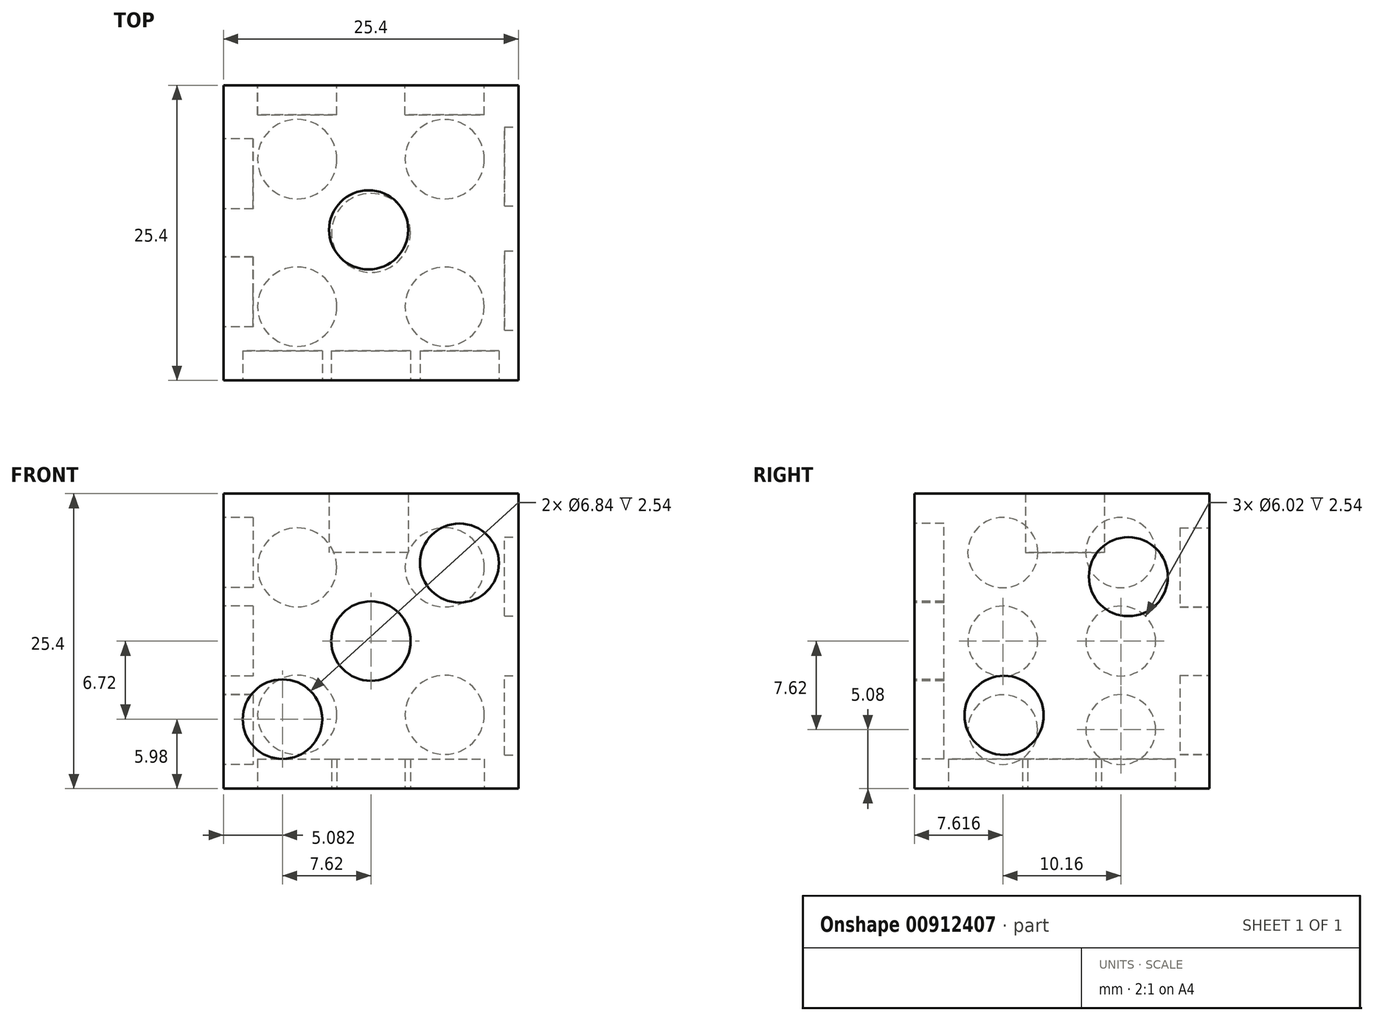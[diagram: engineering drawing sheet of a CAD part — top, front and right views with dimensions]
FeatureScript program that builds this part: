
annotation { "Feature Type Name" : "Feature", "Feature Type Description" : "" }
export const myFeature = defineFeature(function(context is Context, id is Id, definition is map)
    precondition{}
    {
        {
            var Q0;
            Q0=qCreatedBy(makeId("Top.planeOp"),FACE);
            var sketch = newSketch(context, id + "F0", { "sketchPlane" : qUnion([Q0])});
            skLineSegment(sketch, "E0.bottom", {"start": v(-22.93, 8.38) * mm, "end": v(-5.15, 8.38) * mm});
            skLineSegment(sketch, "E0.top", {"start": v(-22.93, -17.02) * mm, "end": v(-5.15, -17.02) * mm});
            skLineSegment(sketch, "E0.left", {"start": v(-26.74, 4.57) * mm, "end": v(-26.74, -13.21) * mm});
            skLineSegment(sketch, "E0.right", {"start": v(-1.34, 4.57) * mm, "end": v(-1.34, -13.21) * mm});
            skLineSegment(sketch, "E1.bottom", {"start": v(-15, 3.03) * mm, "end": v(-14.46, 3.03) * mm});
            skCircle(sketch, "E2", {"center": v(-14.24, -4.06) * mm, "radius": 3.4 * mm});
            skPoint(sketch, "E3.visualSharp", {"position": v(-26.74, 8.38) * mm});
            skPoint(sketch, "E4.visualSharp", {"position": v(-26.74, -17.02) * mm});
            skPoint(sketch, "E5.visualSharp", {"position": v(-1.34, -17.02) * mm});
            skPoint(sketch, "E6.visualSharp", {"position": v(-1.34, 8.38) * mm});
            skLineSegment(sketch, "E7", {"start": v(-26.74, -13.21) * mm, "end": v(-26.74, -17.02) * mm});
            skLineSegment(sketch, "E8", {"start": v(-26.74, -17.02) * mm, "end": v(-22.93, -17.02) * mm});
            skLineSegment(sketch, "E9", {"start": v(-1.34, -17.02) * mm, "end": v(-1.34, -13.21) * mm});
            skLineSegment(sketch, "E10", {"start": v(-5.15, -17.02) * mm, "end": v(-1.34, -17.02) * mm});
            skLineSegment(sketch, "E11", {"start": v(-1.34, 4.57) * mm, "end": v(-1.34, 8.38) * mm});
            skLineSegment(sketch, "E12", {"start": v(-4.55, 8.33) * mm, "end": v(-5.15, 8.38) * mm});
            skLineSegment(sketch, "E13", {"start": v(-1.34, 8.38) * mm, "end": v(-5.15, 8.38) * mm});
            skLineSegment(sketch, "E14", {"start": v(-22.93, 8.38) * mm, "end": v(-26.74, 8.38) * mm});
            skLineSegment(sketch, "E15", {"start": v(-26.74, 4.57) * mm, "end": v(-26.74, 8.38) * mm});
            skSolve(sketch);
        }
        {
            var Q0;
            Q0=qSketchRegion(id+"F0",true);
            extrude(context, id + "F1", {"entities" : qUnion([Q0]), "depth" : 25.4 * mm, "offsetDistance" : 25.4 * mm});
        }
        {
            var Q0;
            Q0=qCreatedBy(makeId("Right.planeOp"),FACE);
            var sketch = newSketch(context, id + "F2", { "sketchPlane" : qUnion([Q0])});
            skCircle(sketch, "E16", {"center": v(-9.3, 6.3) * mm, "radius": 3.4 * mm});
            skCircle(sketch, "E17", {"center": v(1.4, 18.25) * mm, "radius": 3.4 * mm});
            skSolve(sketch);
        }
        {
            var Q0;
            Q0=makeQuery(id+"F0.imprint","IMPRINT",FACE,{"disambiguationData":[TD([[makeQuery(id+"F0.imprint","IMPRINT",EDGE,{"derivedFrom":sQuery(id+"F0.wireOp",EDGE,"E2")}),1.0]])]});
            extrude(context, id + "F3", {"entities" : qUnion([Q0]), "operationType" : NewBodyOperationType.ADD, "depth" : 20.32 * mm, "offsetDistance" : 25.4 * mm});
        }
        {
            var Q0;
            Q0=makeQuery(id+"F1.opExtrude","SWEPT_FACE",FACE,{"disambiguationData":[OSD([sQuery(id+"F0.wireOp",EDGE,"E0.top")])]});
            var sketch = newSketch(context, id + "F4", { "sketchPlane" : qUnion([Q0])});
            skCircle(sketch, "E18", {"center": v(-21.66, 5.98) * mm, "radius": 3.42 * mm});
            skCircle(sketch, "E19", {"center": v(-6.42, 19.42) * mm, "radius": 3.4 * mm});
            skCircle(sketch, "E20", {"center": v(-14.04, 12.7) * mm, "radius": 3.42 * mm});
            skSolve(sketch);
        }
        {
            var Q0;
            Q0=makeQuery(id+"F4.imprint","IMPRINT",FACE,{"disambiguationData":[TD([[makeQuery(id+"F4.imprint","IMPRINT",EDGE,{"derivedFrom":sQuery(id+"F4.wireOp",EDGE,"E18")}),1.0]])]});
            var Q1;
            Q1=makeQuery(id+"F4.imprint","IMPRINT",FACE,{"disambiguationData":[TD([[makeQuery(id+"F4.imprint","IMPRINT",EDGE,{"derivedFrom":sQuery(id+"F4.wireOp",EDGE,"E20")}),1.0]])]});
            var Q2;
            Q2=makeQuery(id+"F4.imprint","IMPRINT",FACE,{"disambiguationData":[TD([[makeQuery(id+"F4.imprint","IMPRINT",EDGE,{"derivedFrom":sQuery(id+"F4.wireOp",EDGE,"E19")}),1.0]])]});
            extrude(context, id + "F5", {"entities" : qUnion([Q0, Q1, Q2]), "operationType" : NewBodyOperationType.REMOVE, "oppositeDirection" : true, "depth" : 2.54 * mm, "offsetDistance" : 25.4 * mm});
        }
        {
            var Q0;
            Q0=makeQuery(id+"F1.opExtrude","SWEPT_FACE",FACE,{"disambiguationData":[OSD([sQuery(id+"F0.wireOp",EDGE,"E0.bottom")])]});
            var sketch = newSketch(context, id + "F6", { "sketchPlane" : qUnion([Q0])});
            skLineSegment(sketch, "E21", {"start": v(14.04, 25.4) * mm, "end": v(14.04, 0) * mm});
            skPoint(sketch, "E22.endSnap0", {"position": v(20.39, 19.05) * mm});
            skPoint(sketch, "E23.endSnap0", {"position": v(7.69, 6.35) * mm});
            skCircle(sketch, "E24", {"center": v(7.69, 6.35) * mm, "radius": 3.4 * mm});
            skCircle(sketch, "E25", {"center": v(20.39, 6.35) * mm, "radius": 3.4 * mm});
            skCircle(sketch, "E26", {"center": v(20.39, 19.05) * mm, "radius": 3.4 * mm});
            skCircle(sketch, "E27", {"center": v(7.69, 19.05) * mm, "radius": 3.4 * mm});
            skSolve(sketch);
        }
        {
            var Q0;
            Q0=makeQuery(id+"F6.imprint","IMPRINT",FACE,{"disambiguationData":[TD([[makeQuery(id+"F6.imprint","IMPRINT",EDGE,{"derivedFrom":sQuery(id+"F6.wireOp",EDGE,"E27")}),1.0]])]});
            var Q1;
            Q1=makeQuery(id+"F6.imprint","IMPRINT",FACE,{"disambiguationData":[TD([[makeQuery(id+"F6.imprint","IMPRINT",EDGE,{"derivedFrom":sQuery(id+"F6.wireOp",EDGE,"E25")}),1.0]])]});
            var Q2;
            Q2=makeQuery(id+"F6.imprint","IMPRINT",FACE,{"disambiguationData":[TD([[makeQuery(id+"F6.imprint","IMPRINT",EDGE,{"derivedFrom":sQuery(id+"F6.wireOp",EDGE,"E26")}),1.0]])]});
            var Q3;
            Q3=makeQuery(id+"F6.imprint","IMPRINT",FACE,{"disambiguationData":[TD([[makeQuery(id+"F6.imprint","IMPRINT",EDGE,{"derivedFrom":sQuery(id+"F6.wireOp",EDGE,"E24")}),1.0]])]});
            extrude(context, id + "F7", {"entities" : qUnion([Q0, Q1, Q2, Q3]), "operationType" : NewBodyOperationType.REMOVE, "oppositeDirection" : true, "depth" : 2.54 * mm, "offsetDistance" : 25.4 * mm});
        }
        {
            var Q0;
            {var subQ0=sQuery(id+"F0.wireOp",EDGE,"E2");Q0=makeQuery(id+"F3.boolean.opBoolean","MERGE",FACE,{"derivedFrom":[makeQuery(id+"F1.opExtrude","CAP_FACE",FACE,{"disambiguationData":[OSD([sQuery(id+"F0.wireOp",EDGE,"E0.bottom"),sQuery(id+"F0.wireOp",EDGE,"E0.top"),sQuery(id+"F0.wireOp",EDGE,"E0.left"),sQuery(id+"F0.wireOp",EDGE,"E0.right"),subQ0])],"isStart":true}),makeQuery(id+"F3.opExtrude","CAP_FACE",FACE,{"disambiguationData":[OSD([subQ0])],"isStart":true})]});}
            var sketch = newSketch(context, id + "F8", { "sketchPlane" : qUnion([Q0])});
            skPoint(sketch, "E28.oppositeSnap0", {"position": v(-26.74, 4.32) * mm});
            skCircle(sketch, "E29", {"center": v(-14.04, 4.32) * mm, "radius": 3.4 * mm});
            skPoint(sketch, "E30.endSnap0", {"position": v(-14.04, -8.38) * mm});
            skCircle(sketch, "E31", {"center": v(-20.39, 10.67) * mm, "radius": 3.42 * mm});
            skCircle(sketch, "E32", {"center": v(-7.69, 10.67) * mm, "radius": 3.4 * mm});
            skCircle(sketch, "E33", {"center": v(-7.69, -2.03) * mm, "radius": 3.42 * mm});
            skCircle(sketch, "E34", {"center": v(-20.39, -2.03) * mm, "radius": 3.42 * mm});
            skLineSegment(sketch, "E35", {"start": v(-14.04, 4.32) * mm, "end": v(-26.74, 4.32) * mm});
            skLineSegment(sketch, "E36", {"start": v(-20.39, 4.32) * mm, "end": v(-20.39, 17.02) * mm});
            skLineSegment(sketch, "E37", {"start": v(-20.39, 4.32) * mm, "end": v(-20.39, -8.38) * mm});
            skLineSegment(sketch, "E38", {"start": v(-14.04, 4.32) * mm, "end": v(-1.34, 4.32) * mm});
            skLineSegment(sketch, "E39", {"start": v(-7.69, 4.32) * mm, "end": v(-7.69, -8.38) * mm});
            skLineSegment(sketch, "E40", {"start": v(-7.69, 4.32) * mm, "end": v(-7.69, 17.02) * mm});
            skSolve(sketch);
        }
        {
            var Q0;
            Q0=qSketchRegion(id+"F8",true);
            extrude(context, id + "F9", {"entities" : qUnion([Q0]), "operationType" : NewBodyOperationType.REMOVE, "oppositeDirection" : true, "depth" : 2.54 * mm, "offsetDistance" : 25.4 * mm});
        }
        {
            var Q0;
            Q0=makeQuery(id+"F1.opExtrude","SWEPT_FACE",FACE,{"disambiguationData":[OSD([sQuery(id+"F0.wireOp",EDGE,"E0.left")])]});
            var sketch = newSketch(context, id + "F10", { "sketchPlane" : qUnion([Q0])});
            skCircle(sketch, "E41", {"center": v(9.4, 20.32) * mm, "radius": 3.02 * mm});
            skCircle(sketch, "E42", {"center": v(-0.76, 5.08) * mm, "radius": 3.01 * mm});
            skCircle(sketch, "E43", {"center": v(-0.76, 12.7) * mm, "radius": 3 * mm});
            skCircle(sketch, "E44", {"center": v(9.4, 12.7) * mm, "radius": 3.01 * mm});
            skCircle(sketch, "E45", {"center": v(-0.76, 20.32) * mm, "radius": 3.02 * mm});
            skCircle(sketch, "E46", {"center": v(9.4, 5.08) * mm, "radius": 3 * mm});
            skSolve(sketch);
        }
        {
            var Q0;
            Q0=makeQuery(id+"F10.imprint","IMPRINT",FACE,{"disambiguationData":[TD([[makeQuery(id+"F10.imprint","IMPRINT",EDGE,{"derivedFrom":sQuery(id+"F10.wireOp",EDGE,"E41")}),1.0]])]});
            var Q1;
            Q1=makeQuery(id+"F10.imprint","IMPRINT",FACE,{"disambiguationData":[TD([[makeQuery(id+"F10.imprint","IMPRINT",EDGE,{"derivedFrom":sQuery(id+"F10.wireOp",EDGE,"E44")}),1.0]])]});
            var Q2;
            Q2=makeQuery(id+"F10.imprint","IMPRINT",FACE,{"disambiguationData":[TD([[makeQuery(id+"F10.imprint","IMPRINT",EDGE,{"derivedFrom":sQuery(id+"F10.wireOp",EDGE,"E43")}),1.0]])]});
            var Q3;
            Q3=makeQuery(id+"F10.imprint","IMPRINT",FACE,{"disambiguationData":[TD([[makeQuery(id+"F10.imprint","IMPRINT",EDGE,{"derivedFrom":sQuery(id+"F10.wireOp",EDGE,"E45")}),1.0]])]});
            var Q4;
            Q4=makeQuery(id+"F10.imprint","IMPRINT",FACE,{"disambiguationData":[TD([[makeQuery(id+"F10.imprint","IMPRINT",EDGE,{"derivedFrom":sQuery(id+"F10.wireOp",EDGE,"E42")}),1.0]])]});
            var Q5;
            Q5=makeQuery(id+"F10.imprint","IMPRINT",FACE,{"disambiguationData":[TD([[makeQuery(id+"F10.imprint","IMPRINT",EDGE,{"derivedFrom":sQuery(id+"F10.wireOp",EDGE,"E46")}),1.0]])]});
            extrude(context, id + "F11", {"entities" : qUnion([Q0, Q1, Q2, Q3, Q4, Q5]), "operationType" : NewBodyOperationType.REMOVE, "oppositeDirection" : true, "depth" : 2.54 * mm, "offsetDistance" : 25.4 * mm});
        }
        {
            var Q0;
            Q0=makeQuery(id+"F2.imprint","IMPRINT",FACE,{"disambiguationData":[TD([[makeQuery(id+"F2.imprint","IMPRINT",EDGE,{"derivedFrom":sQuery(id+"F2.wireOp",EDGE,"E16")}),1.0]])]});
            var Q1;
            Q1=makeQuery(id+"F2.imprint","IMPRINT",FACE,{"disambiguationData":[TD([[makeQuery(id+"F2.imprint","IMPRINT",EDGE,{"derivedFrom":sQuery(id+"F2.wireOp",EDGE,"E17")}),1.0]])]});
            extrude(context, id + "F12", {"entities" : qUnion([Q0, Q1]), "operationType" : NewBodyOperationType.REMOVE, "oppositeDirection" : true, "depth" : 2.54 * mm, "offsetDistance" : 25.4 * mm});
        }
    });
